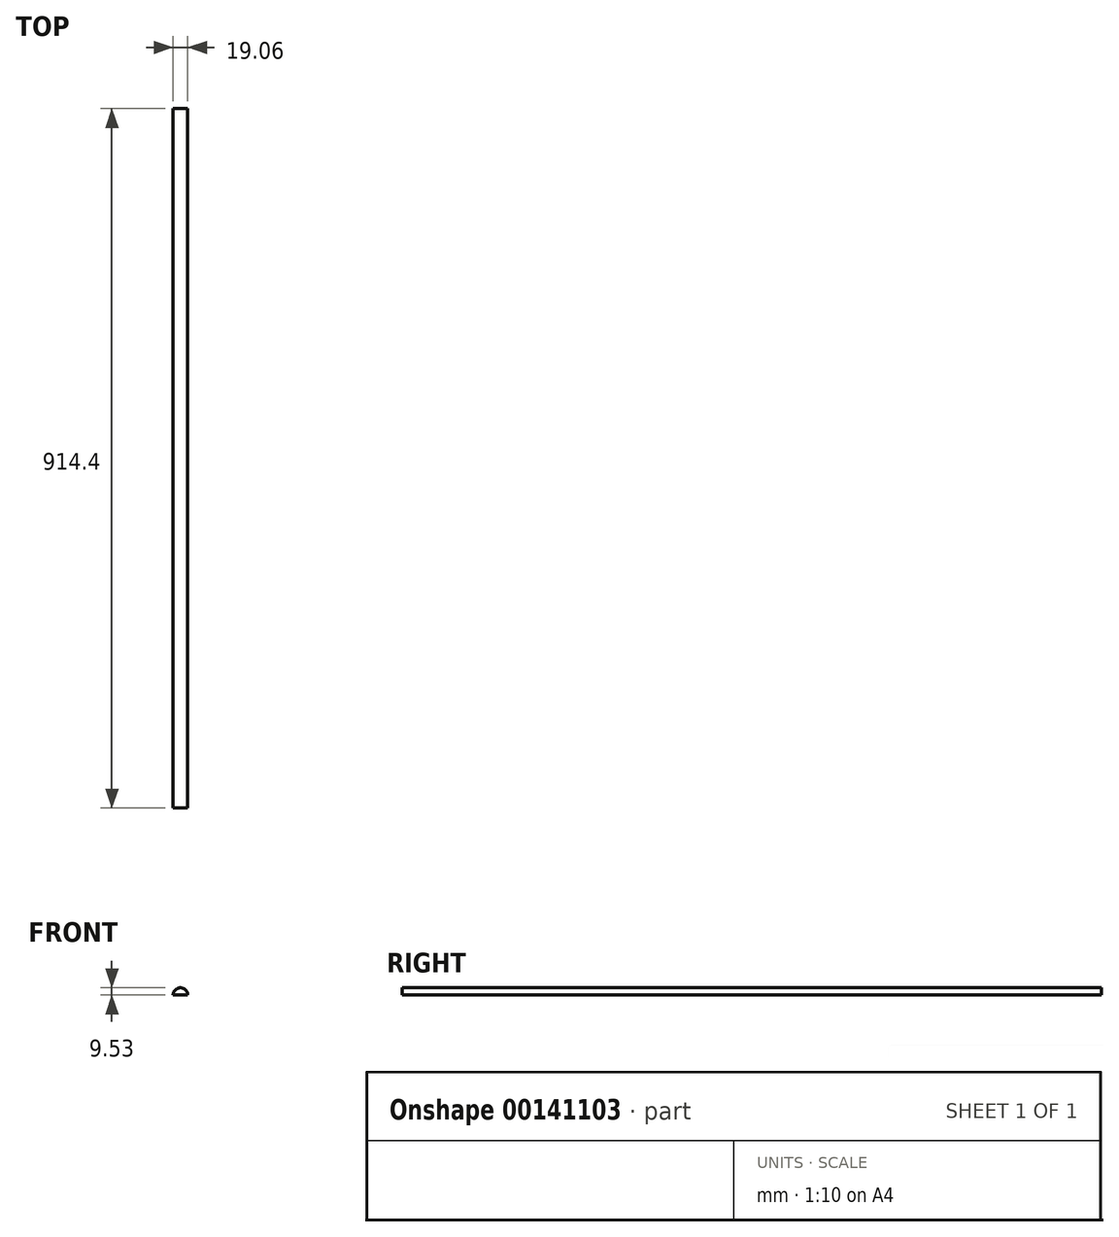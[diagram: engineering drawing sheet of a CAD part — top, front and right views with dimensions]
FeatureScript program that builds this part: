
annotation { "Feature Type Name" : "Feature", "Feature Type Description" : "" }
export const myFeature = defineFeature(function(context is Context, id is Id, definition is map)
    precondition{}
    {
        {
            var Q0;
            Q0=qCreatedBy(makeId("Front.planeOp"),FACE);
            var sketch = newSketch(context, id + "F0", { "sketchPlane" : qUnion([Q0])});
            skArc(sketch, "E0", {"start": v(9.53, 0) * mm, "mid": v(0, 9.53) * mm, "end": v(-9.53, 0) * mm});
            skLineSegment(sketch, "E1", {"start": v(-9.53, 0) * mm, "end": v(9.53, 0) * mm});
            skSolve(sketch);
        }
        {
            var Q0;
            Q0 = qSketchRegion(id + "F0", true);
            extrude(context, id + "F1", {"entities" : qUnion([Q0]), "depth" : 914.4 * mm});
        }
    });
